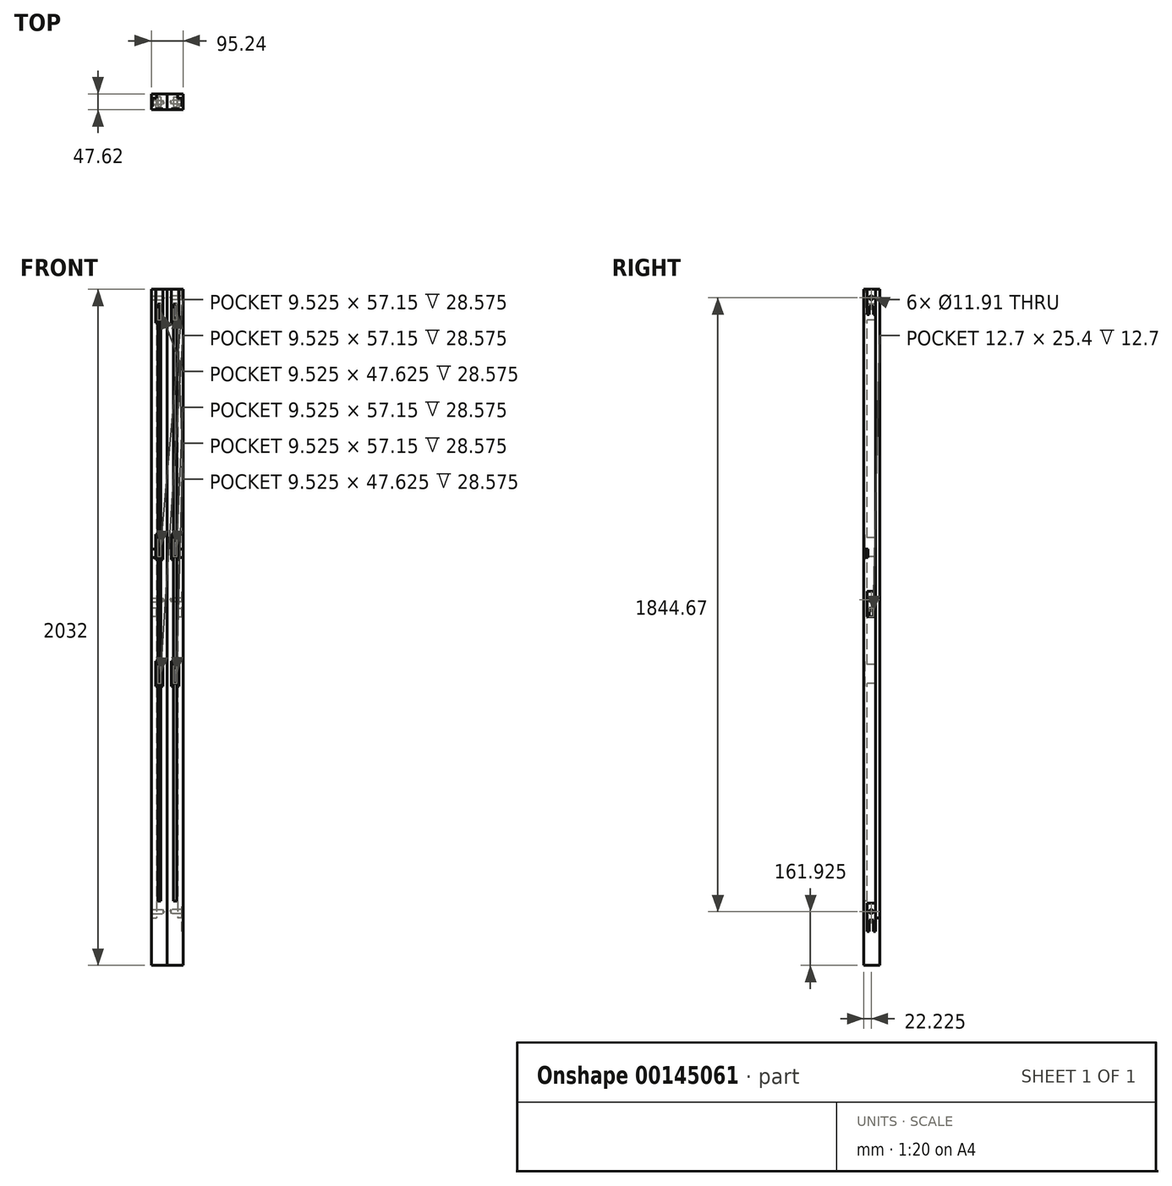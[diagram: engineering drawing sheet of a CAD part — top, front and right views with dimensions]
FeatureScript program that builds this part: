
annotation { "Feature Type Name" : "Feature", "Feature Type Description" : "" }
export const myFeature = defineFeature(function(context is Context, id is Id, definition is map)
    precondition{}
    {
        {
            var Q0;
            Q0=qCreatedBy(makeId("Top.planeOp"),FACE);
            var sketch = newSketch(context, id + "F0", { "sketchPlane" : qUnion([Q0])});
            skLineSegment(sketch, "E0.bottom", {"start": v(0, 0) * mm, "end": v(47.63, 0) * mm});
            skLineSegment(sketch, "E0.top", {"start": v(0, 47.62) * mm, "end": v(47.62, 47.62) * mm});
            skLineSegment(sketch, "E0.left", {"start": v(0, 0) * mm, "end": v(0, 47.62) * mm});
            skLineSegment(sketch, "E0.right", {"start": v(47.63, 0) * mm, "end": v(47.62, 47.62) * mm});
            skSolve(sketch);
        }
        {
            var Q0;
            Q0=makeQuery(id+"F0.imprint","IMPRINT",FACE,{"disambiguationData":[TD([[makeQuery(id+"F0.imprint","IMPRINT",EDGE,{"derivedFrom":sQuery(id+"F0.wireOp",EDGE,"E0.bottom")}),1.0]])]});
            extrude(context, id + "F1", {"entities" : qUnion([Q0]), "depth" : 2032 * mm});
        }
        {
            var Q0;
            Q0=makeQuery(id+"F1.opExtrude","SWEPT_FACE",FACE,{"disambiguationData":[OSD([sQuery(id+"F0.wireOp",EDGE,"E0.bottom")])]});
            var sketch = newSketch(context, id + "F2", { "sketchPlane" : qUnion([Q0])});
            skLineSegment(sketch, "E1.bottom", {"start": v(34.93, 203.2) * mm, "end": v(12.7, 203.2) * mm});
            skLineSegment(sketch, "E1.top", {"start": v(34.93, 101.6) * mm, "end": v(12.7, 101.6) * mm});
            skLineSegment(sketch, "E1.left", {"start": v(34.93, 203.2) * mm, "end": v(34.93, 101.6) * mm});
            skLineSegment(sketch, "E1.right", {"start": v(12.7, 203.2) * mm, "end": v(12.7, 101.6) * mm});
            skPoint(sketch, "E1.middle", {"position": v(23.81, 152.4) * mm});
            skLineSegment(sketch, "E2.bottom", {"start": v(28.58, 101.6) * mm, "end": v(19.05, 101.6) * mm});
            skLineSegment(sketch, "E2.top", {"start": v(28.57, 142.88) * mm, "end": v(19.05, 142.88) * mm});
            skLineSegment(sketch, "E2.left", {"start": v(28.58, 101.6) * mm, "end": v(28.58, 142.88) * mm});
            skLineSegment(sketch, "E2.right", {"start": v(19.05, 101.6) * mm, "end": v(19.05, 142.88) * mm});
            skPoint(sketch, "E2.middle", {"position": v(23.81, 122.24) * mm});
            skLineSegment(sketch, "E3.bottom", {"start": v(12.7, 838.2) * mm, "end": v(34.92, 838.2) * mm});
            skLineSegment(sketch, "E3.top", {"start": v(12.7, 914.4) * mm, "end": v(34.92, 914.4) * mm});
            skLineSegment(sketch, "E3.left", {"start": v(12.7, 838.2) * mm, "end": v(12.7, 914.4) * mm});
            skLineSegment(sketch, "E3.right", {"start": v(34.93, 838.2) * mm, "end": v(34.93, 914.4) * mm});
            skLineSegment(sketch, "E4", {"start": v(19.05, 838.2) * mm, "end": v(19.05, 914.4) * mm});
            skLineSegment(sketch, "E5", {"start": v(28.58, 838.2) * mm, "end": v(28.58, 914.4) * mm});
            skPoint(sketch, "E5.endSnap0", {"position": v(23.81, 914.4) * mm});
            skLineSegment(sketch, "E6.bottom", {"start": v(12.7, 1219.2) * mm, "end": v(34.92, 1219.2) * mm});
            skLineSegment(sketch, "E6.top", {"start": v(12.7, 1295.4) * mm, "end": v(34.92, 1295.4) * mm});
            skLineSegment(sketch, "E6.left", {"start": v(12.7, 1219.2) * mm, "end": v(12.7, 1295.4) * mm});
            skLineSegment(sketch, "E6.right", {"start": v(34.92, 1219.2) * mm, "end": v(34.92, 1295.4) * mm});
            skLineSegment(sketch, "E7", {"start": v(19.05, 1219.2) * mm, "end": v(19.05, 1295.4) * mm});
            skLineSegment(sketch, "E8", {"start": v(28.57, 1219.2) * mm, "end": v(28.57, 1295.4) * mm});
            skLineSegment(sketch, "E9.bottom", {"start": v(12.7, 1930.4) * mm, "end": v(34.92, 1930.4) * mm});
            skLineSegment(sketch, "E9.top", {"start": v(12.7, 2032) * mm, "end": v(34.92, 2032) * mm});
            skLineSegment(sketch, "E9.left", {"start": v(12.7, 1930.4) * mm, "end": v(12.7, 2032) * mm});
            skLineSegment(sketch, "E9.right", {"start": v(34.92, 1930.4) * mm, "end": v(34.92, 2032) * mm});
            skLineSegment(sketch, "E10", {"start": v(19.05, 1930.4) * mm, "end": v(19.05, 2032) * mm});
            skLineSegment(sketch, "E11", {"start": v(28.57, 1930.4) * mm, "end": v(28.57, 2032) * mm});
            skLineSegment(sketch, "E12", {"start": v(19.05, 1987.55) * mm, "end": v(28.57, 1987.55) * mm});
            skLineSegment(sketch, "E13.bottom", {"start": v(19.05, 193.68) * mm, "end": v(28.57, 193.68) * mm});
            skLineSegment(sketch, "E13.top", {"start": v(19.05, 1939.93) * mm, "end": v(28.57, 1939.93) * mm});
            skLineSegment(sketch, "E13.left", {"start": v(19.05, 193.68) * mm, "end": v(19.05, 1939.93) * mm});
            skLineSegment(sketch, "E13.right", {"start": v(28.57, 193.68) * mm, "end": v(28.57, 1939.93) * mm});
            skLineSegment(sketch, "E14", {"start": v(19.05, 847.73) * mm, "end": v(28.57, 847.73) * mm});
            skLineSegment(sketch, "E15", {"start": v(19.05, 904.88) * mm, "end": v(28.57, 904.88) * mm});
            skLineSegment(sketch, "E16", {"start": v(19.05, 1228.73) * mm, "end": v(28.57, 1228.73) * mm});
            skLineSegment(sketch, "E17", {"start": v(19.05, 1285.88) * mm, "end": v(28.57, 1285.88) * mm});
            skSolve(sketch);
        }
        {
            var Q0;
            Q0=makeQuery(id+"F2.imprint","IMPRINT",FACE,{"disambiguationData":[TD([[makeQuery(id+"F2.imprint","IMPRINT",EDGE,{"derivedFrom":sQuery(id+"F2.wireOp",EDGE,"E2.bottom")}),-1.0]])]});
            var Q1;
            {var subQ2=sQuery(id+"F2.wireOp",EDGE,"E12");Q1=makeQuery(id+"F2.imprint","IMPRINT",FACE,{"disambiguationData":[TD([[makeQuery(id+"F2.imprint","IMPRINT",EDGE,{"derivedFrom":subQ2}),-1.0]])]});}
            var Q2;
            {var subQ0=sQuery(id+"F2.wireOp",EDGE,"E14");Q2=makeQuery(id+"F2.imprint","IMPRINT",FACE,{"disambiguationData":[TD([[makeQuery(id+"F2.imprint","IMPRINT",EDGE,{"derivedFrom":subQ0}),1.0]])]});}
            var Q3;
            {var subQ0=sQuery(id+"F2.wireOp",EDGE,"E16");Q3=makeQuery(id+"F2.imprint","IMPRINT",FACE,{"disambiguationData":[TD([[makeQuery(id+"F2.imprint","IMPRINT",EDGE,{"derivedFrom":subQ0}),1.0]])]});}
            extrude(context, id + "F3", {"entities" : qUnion([Q0, Q1, Q2, Q3]), "operationType" : NewBodyOperationType.REMOVE, "oppositeDirection" : true, "depth" : 38.1 * mm});
        }
        {
            var Q0;
            {var subQ5=sQuery(id+"F2.wireOp",EDGE,"E13.bottom");Q0=makeQuery(id+"F2.imprint","IMPRINT",FACE,{"disambiguationData":[TD([[makeQuery(id+"F2.imprint","IMPRINT",EDGE,{"derivedFrom":subQ5}),1.0]])]});}
            var Q1;
            {var subQ0=sQuery(id+"F2.wireOp",EDGE,"E13.right");var subQ1=sQuery(id+"F2.wireOp",EDGE,"E1.bottom");var subQ2=makeQuery(id+"F2.imprint","INTERSECT",VERTEX,{"derivedFrom":[subQ1,subQ0]});Q1=makeQuery(id+"F2.imprint","IMPRINT",FACE,{"disambiguationData":[TD([[makeQuery(id+"F2.imprint","IMPRINT",EDGE,{"disambiguationData":[TD([[subQ2,-1.0]])],"derivedFrom":subQ1}),-1.0]])]});}
            var Q2;
            {var subQ0=sQuery(id+"F2.wireOp",EDGE,"E13.left");var subQ1=sQuery(id+"F2.wireOp",EDGE,"E3.top");var subQ2=makeQuery(id+"F2.imprint","INTERSECT",VERTEX,{"derivedFrom":[subQ1,subQ0]});Q2=makeQuery(id+"F2.imprint","IMPRINT",FACE,{"disambiguationData":[TD([[makeQuery(id+"F2.imprint","IMPRINT",EDGE,{"disambiguationData":[TD([[subQ2,-1.0]])],"derivedFrom":subQ1}),1.0]])]});}
            var Q3;
            {var subQ0=sQuery(id+"F2.wireOp",EDGE,"E13.left");var subQ1=sQuery(id+"F2.wireOp",EDGE,"E6.top");var subQ2=makeQuery(id+"F2.imprint","INTERSECT",VERTEX,{"derivedFrom":[subQ1,subQ0]});Q3=makeQuery(id+"F2.imprint","IMPRINT",FACE,{"disambiguationData":[TD([[makeQuery(id+"F2.imprint","IMPRINT",EDGE,{"disambiguationData":[TD([[subQ2,-1.0]])],"derivedFrom":subQ1}),1.0]])]});}
            var Q4;
            {var subQ5=sQuery(id+"F2.wireOp",EDGE,"E13.top");Q4=makeQuery(id+"F2.imprint","IMPRINT",FACE,{"disambiguationData":[TD([[makeQuery(id+"F2.imprint","IMPRINT",EDGE,{"derivedFrom":subQ5}),-1.0]])]});}
            var Q5;
            {var subQ5=sQuery(id+"F2.wireOp",EDGE,"E16");Q5=makeQuery(id+"F2.imprint","IMPRINT",FACE,{"disambiguationData":[TD([[makeQuery(id+"F2.imprint","IMPRINT",EDGE,{"derivedFrom":subQ5}),-1.0]])]});}
            var Q6;
            {var subQ5=sQuery(id+"F2.wireOp",EDGE,"E14");Q6=makeQuery(id+"F2.imprint","IMPRINT",FACE,{"disambiguationData":[TD([[makeQuery(id+"F2.imprint","IMPRINT",EDGE,{"derivedFrom":subQ5}),-1.0]])]});}
            var Q7;
            {var subQ5=sQuery(id+"F2.wireOp",EDGE,"E17");Q7=makeQuery(id+"F2.imprint","IMPRINT",FACE,{"disambiguationData":[TD([[makeQuery(id+"F2.imprint","IMPRINT",EDGE,{"derivedFrom":subQ5}),1.0]])]});}
            var Q8;
            {var subQ5=sQuery(id+"F2.wireOp",EDGE,"E15");Q8=makeQuery(id+"F2.imprint","IMPRINT",FACE,{"disambiguationData":[TD([[makeQuery(id+"F2.imprint","IMPRINT",EDGE,{"derivedFrom":subQ5}),1.0]])]});}
            extrude(context, id + "F4", {"entities" : qUnion([Q0, Q1, Q2, Q3, Q4, Q5, Q6, Q7, Q8]), "operationType" : NewBodyOperationType.REMOVE, "oppositeDirection" : true, "depth" : 9.52 * mm});
        }
        {
            var Q0;
            {var subQ0=sQuery(id+"F2.wireOp",EDGE,"E9.left");Q0=makeQuery(id+"F2.imprint","IMPRINT",FACE,{"disambiguationData":[TD([[makeQuery(id+"F2.imprint","IMPRINT",EDGE,{"derivedFrom":subQ0}),-1.0]])]});}
            var Q1;
            {var subQ5=sQuery(id+"F2.wireOp",EDGE,"E12");Q1=makeQuery(id+"F2.imprint","IMPRINT",FACE,{"disambiguationData":[TD([[makeQuery(id+"F2.imprint","IMPRINT",EDGE,{"derivedFrom":subQ5}),1.0]])]});}
            var Q2;
            {var subQ4=sQuery(id+"F2.wireOp",EDGE,"E9.right");Q2=makeQuery(id+"F2.imprint","IMPRINT",FACE,{"disambiguationData":[TD([[makeQuery(id+"F2.imprint","IMPRINT",EDGE,{"derivedFrom":subQ4}),1.0]])]});}
            var Q3;
            {var subQ4=sQuery(id+"F2.wireOp",EDGE,"E6.left");Q3=makeQuery(id+"F2.imprint","IMPRINT",FACE,{"disambiguationData":[TD([[makeQuery(id+"F2.imprint","IMPRINT",EDGE,{"derivedFrom":subQ4}),-1.0]])]});}
            var Q4;
            {var subQ0=sQuery(id+"F2.wireOp",EDGE,"E6.right");Q4=makeQuery(id+"F2.imprint","IMPRINT",FACE,{"disambiguationData":[TD([[makeQuery(id+"F2.imprint","IMPRINT",EDGE,{"derivedFrom":subQ0}),1.0]])]});}
            var Q5;
            {var subQ0=sQuery(id+"F2.wireOp",EDGE,"E3.left");Q5=makeQuery(id+"F2.imprint","IMPRINT",FACE,{"disambiguationData":[TD([[makeQuery(id+"F2.imprint","IMPRINT",EDGE,{"derivedFrom":subQ0}),-1.0]])]});}
            var Q6;
            {var subQ4=sQuery(id+"F2.wireOp",EDGE,"E3.right");Q6=makeQuery(id+"F2.imprint","IMPRINT",FACE,{"disambiguationData":[TD([[makeQuery(id+"F2.imprint","IMPRINT",EDGE,{"derivedFrom":subQ4}),1.0]])]});}
            var Q7;
            {var subQ2=sQuery(id+"F2.wireOp",EDGE,"E1.left");Q7=makeQuery(id+"F2.imprint","IMPRINT",FACE,{"disambiguationData":[TD([[makeQuery(id+"F2.imprint","IMPRINT",EDGE,{"derivedFrom":subQ2}),-1.0]])]});}
            extrude(context, id + "F5", {"entities" : qUnion([Q0, Q1, Q2, Q3, Q4, Q5, Q6, Q7]), "operationType" : NewBodyOperationType.REMOVE, "flatOperationType" : FlatOperationType.REMOVE, "oppositeDirection" : true, "offsetDistance" : 25.4 * mm, "depth" : 3.17 * mm, "domain" : OperationDomain.MODEL});
        }
        {
            var Q0;
            Q0=makeQuery(id+"F1.opExtrude","SWEPT_FACE",FACE,{"disambiguationData":[OSD([sQuery(id+"F0.wireOp",EDGE,"E0.right")])]});
            var sketch = newSketch(context, id + "F6", { "sketchPlane" : qUnion([Q0])});
            skLineSegment(sketch, "E18.bottom", {"start": v(34.92, 101.6) * mm, "end": v(9.52, 101.6) * mm});
            skLineSegment(sketch, "E18.top", {"start": v(34.92, 187.33) * mm, "end": v(9.52, 187.33) * mm});
            skLineSegment(sketch, "E18.left", {"start": v(34.92, 101.6) * mm, "end": v(34.92, 187.33) * mm});
            skLineSegment(sketch, "E18.right", {"start": v(9.52, 101.6) * mm, "end": v(9.52, 187.33) * mm});
            skPoint(sketch, "E18.middle", {"position": v(22.22, 144.46) * mm});
            skLineSegment(sketch, "E19", {"start": v(22.22, 144.46) * mm, "end": v(22.22, 187.33) * mm, "construction": true});
            skPoint(sketch, "E20", {"position": v(22.22, 161.93) * mm});
            skLineSegment(sketch, "E21.bottom", {"start": v(28.57, 101.6) * mm, "end": v(15.87, 101.6) * mm});
            skLineSegment(sketch, "E21.top", {"start": v(28.57, 136.53) * mm, "end": v(15.87, 136.53) * mm});
            skLineSegment(sketch, "E21.left", {"start": v(28.57, 101.6) * mm, "end": v(28.57, 136.53) * mm});
            skLineSegment(sketch, "E21.right", {"start": v(15.87, 101.6) * mm, "end": v(15.87, 136.53) * mm});
            skPoint(sketch, "E21.middle", {"position": v(22.22, 119.06) * mm});
            skLineSegment(sketch, "E22.bottom", {"start": v(9.52, 1955.8) * mm, "end": v(34.92, 1955.8) * mm});
            skLineSegment(sketch, "E22.top", {"start": v(9.52, 2032) * mm, "end": v(34.92, 2032) * mm});
            skLineSegment(sketch, "E22.left", {"start": v(9.52, 1955.8) * mm, "end": v(9.52, 2032) * mm});
            skLineSegment(sketch, "E22.right", {"start": v(34.92, 1955.8) * mm, "end": v(34.92, 2032) * mm});
            skPoint(sketch, "E22.middle", {"position": v(22.22, 1993.9) * mm});
            skLineSegment(sketch, "E23", {"start": v(22.22, 2032) * mm, "end": v(22.22, 1993.9) * mm, "construction": true});
            skPoint(sketch, "E23.startSnap0", {"position": v(22.22, 2032) * mm});
            skPoint(sketch, "E24", {"position": v(22.22, 2006.6) * mm});
            skLineSegment(sketch, "E25.bottom", {"start": v(15.87, 1955.8) * mm, "end": v(28.57, 1955.8) * mm});
            skLineSegment(sketch, "E25.top", {"start": v(15.87, 1981.2) * mm, "end": v(28.57, 1981.2) * mm});
            skLineSegment(sketch, "E25.left", {"start": v(15.87, 1955.8) * mm, "end": v(15.87, 1981.2) * mm});
            skLineSegment(sketch, "E25.right", {"start": v(28.57, 1955.8) * mm, "end": v(28.57, 1981.2) * mm});
            skPoint(sketch, "E25.middle", {"position": v(22.22, 1968.5) * mm});
            skLineSegment(sketch, "E26.bottom", {"start": v(9.52, 1047.75) * mm, "end": v(34.93, 1047.75) * mm});
            skLineSegment(sketch, "E26.top", {"start": v(9.52, 1123.95) * mm, "end": v(34.93, 1123.95) * mm});
            skLineSegment(sketch, "E26.left", {"start": v(9.52, 1047.75) * mm, "end": v(9.52, 1123.95) * mm});
            skLineSegment(sketch, "E26.right", {"start": v(34.92, 1047.75) * mm, "end": v(34.92, 1123.95) * mm});
            skLineSegment(sketch, "E27", {"start": v(15.87, 1047.75) * mm, "end": v(15.87, 1073.15) * mm});
            skLineSegment(sketch, "E28", {"start": v(15.88, 1073.15) * mm, "end": v(28.57, 1073.15) * mm});
            skLineSegment(sketch, "E29", {"start": v(28.57, 1073.15) * mm, "end": v(28.57, 1047.75) * mm});
            skLineSegment(sketch, "E30", {"start": v(22.22, 1047.75) * mm, "end": v(22.22, 1123.95) * mm, "construction": true});
            skPoint(sketch, "E31", {"position": v(22.22, 1098.55) * mm});
            skSolve(sketch);
        }
        {
            var Q0;
            Q0=sQuery(id+"F6.wireOp",VERTEX,"E24");
            var Q1;
            Q1=sQuery(id+"F6.wireOp",VERTEX,"E20");
            var Q2;
            Q2=sQuery(id+"F6.wireOp",VERTEX,"E31");
            var Q3;
            Q3=makeQuery(id+"F1.opExtrude","SWEPT_BODY",BODY,{"disambiguationData":[OSD([sQuery(id+"F0.wireOp",EDGE,"E0.bottom"),sQuery(id+"F0.wireOp",EDGE,"E0.top"),sQuery(id+"F0.wireOp",EDGE,"E0.left"),sQuery(id+"F0.wireOp",EDGE,"E0.right")])]});
            hole(context, id + "F7", {"style" : HoleStyle.SIMPLE, "endStyle" : HoleEndStyle.BLIND, "holeDiameter" : 11.9 * mm, "holeDepth" : 34.92 * mm, "locations" : qUnion([Q0, Q1, Q2]), "scope" : qUnion([Q3]), "tappedDepth" : 12.7 * mm, "tapClearance" : 3, "startStyle" : HoleStartStyle.PART});
        }
        {
            var Q0;
            Q0=makeQuery(id+"F6.imprint","IMPRINT",FACE,{"disambiguationData":[TD([[makeQuery(id+"F6.imprint","IMPRINT",EDGE,{"derivedFrom":sQuery(id+"F6.wireOp",EDGE,"E25.bottom")}),1.0]])]});
            var Q1;
            Q1=makeQuery(id+"F6.imprint","IMPRINT",FACE,{"disambiguationData":[TD([[makeQuery(id+"F6.imprint","IMPRINT",EDGE,{"derivedFrom":sQuery(id+"F6.wireOp",EDGE,"E21.bottom")}),-1.0]])]});
            var Q2;
            {var subQ0=sQuery(id+"F6.wireOp",EDGE,"E27");Q2=makeQuery(id+"F6.imprint","IMPRINT",FACE,{"disambiguationData":[TD([[makeQuery(id+"F6.imprint","IMPRINT",EDGE,{"derivedFrom":subQ0}),-1.0]])]});}
            extrude(context, id + "F8", {"entities" : qUnion([Q0, Q1, Q2]), "operationType" : NewBodyOperationType.REMOVE, "oppositeDirection" : true, "depth" : 15.88 * mm});
        }
        {
            var Q0;
            Q0=makeQuery(id+"F6.imprint","IMPRINT",FACE,{"disambiguationData":[TD([[makeQuery(id+"F6.imprint","IMPRINT",EDGE,{"derivedFrom":sQuery(id+"F6.wireOp",EDGE,"E18.top")}),1.0]])]});
            var Q1;
            Q1=makeQuery(id+"F6.imprint","IMPRINT",FACE,{"disambiguationData":[TD([[makeQuery(id+"F6.imprint","IMPRINT",EDGE,{"derivedFrom":sQuery(id+"F6.wireOp",EDGE,"E22.top")}),-1.0]])]});
            var Q2;
            Q2=makeQuery(id+"F6.imprint","IMPRINT",FACE,{"disambiguationData":[TD([[makeQuery(id+"F6.imprint","IMPRINT",EDGE,{"derivedFrom":sQuery(id+"F6.wireOp",EDGE,"E26.top")}),-1.0]])]});
            extrude(context, id + "F9", {"entities" : qUnion([Q0, Q1, Q2]), "operationType" : NewBodyOperationType.REMOVE, "oppositeDirection" : true, "depth" : 3.17 * mm});
        }
        {
            var Q0;
            Q0=makeQuery(id+"F1.opExtrude","SWEPT_FACE",FACE,{"disambiguationData":[OSD([sQuery(id+"F0.wireOp",EDGE,"E0.top")])]});
            var sketch = newSketch(context, id + "F10", { "sketchPlane" : qUnion([Q0])});
            skLineSegment(sketch, "E32.bottom", {"start": v(-47.63, 2032) * mm, "end": v(-31.75, 2032) * mm});
            skLineSegment(sketch, "E32.top", {"start": v(-47.62, 142.88) * mm, "end": v(-31.75, 142.88) * mm});
            skLineSegment(sketch, "E32.left", {"start": v(-47.63, 2032) * mm, "end": v(-47.62, 142.87) * mm});
            skLineSegment(sketch, "E32.right", {"start": v(-31.75, 2032) * mm, "end": v(-31.75, 142.87) * mm});
            skSolve(sketch);
        }
        {
            var Q0;
            Q0=makeQuery(id+"F10.imprint","IMPRINT",FACE,{"disambiguationData":[TD([[makeQuery(id+"F10.imprint","IMPRINT",EDGE,{"derivedFrom":sQuery(id+"F10.wireOp",EDGE,"E32.bottom")}),1.0]])]});
            extrude(context, id + "F11", {"entities" : qUnion([Q0]), "operationType" : NewBodyOperationType.REMOVE, "oppositeDirection" : true, "depth" : 12.7 * mm});
        }
        {
            var Q0;
            Q0=makeQuery(id+"F1.opExtrude","SWEPT_FACE",FACE,{"disambiguationData":[OSD([sQuery(id+"F0.wireOp",EDGE,"E0.bottom")])]});
            var sketch = newSketch(context, id + "F12", { "sketchPlane" : qUnion([Q0])});
            skLineSegment(sketch, "E33.bottom", {"start": v(34.92, 1225.55) * mm, "end": v(47.63, 1225.55) * mm});
            skLineSegment(sketch, "E33.top", {"start": v(34.92, 1250.95) * mm, "end": v(47.63, 1250.95) * mm});
            skLineSegment(sketch, "E33.left", {"start": v(34.92, 1225.55) * mm, "end": v(34.92, 1250.95) * mm});
            skLineSegment(sketch, "E33.right", {"start": v(47.63, 1225.55) * mm, "end": v(47.63, 1250.95) * mm});
            skSolve(sketch);
        }
        {
            var Q0;
            Q0=makeQuery(id+"F12.imprint","IMPRINT",FACE,{"disambiguationData":[TD([[makeQuery(id+"F12.imprint","IMPRINT",EDGE,{"derivedFrom":sQuery(id+"F12.wireOp",EDGE,"E33.bottom")}),1.0]])]});
            extrude(context, id + "F13", {"entities" : qUnion([Q0]), "operationType" : NewBodyOperationType.REMOVE, "oppositeDirection" : true, "depth" : 12.7 * mm});
        }
        {
            var Q0;
            Q0=makeQuery(id+"F1.opExtrude","SWEPT_BODY",BODY,{"disambiguationData":[OSD([sQuery(id+"F0.wireOp",EDGE,"E0.bottom"),sQuery(id+"F0.wireOp",EDGE,"E0.top"),sQuery(id+"F0.wireOp",EDGE,"E0.left"),sQuery(id+"F0.wireOp",EDGE,"E0.right")])]});
            var Q1;
            Q1=qCreatedBy(makeId("Right.planeOp"),FACE);
            mirror(context, id + "F14", {"entities" : qUnion([Q0]), "mirrorPlane" : qUnion([Q1])});
        }
    });
